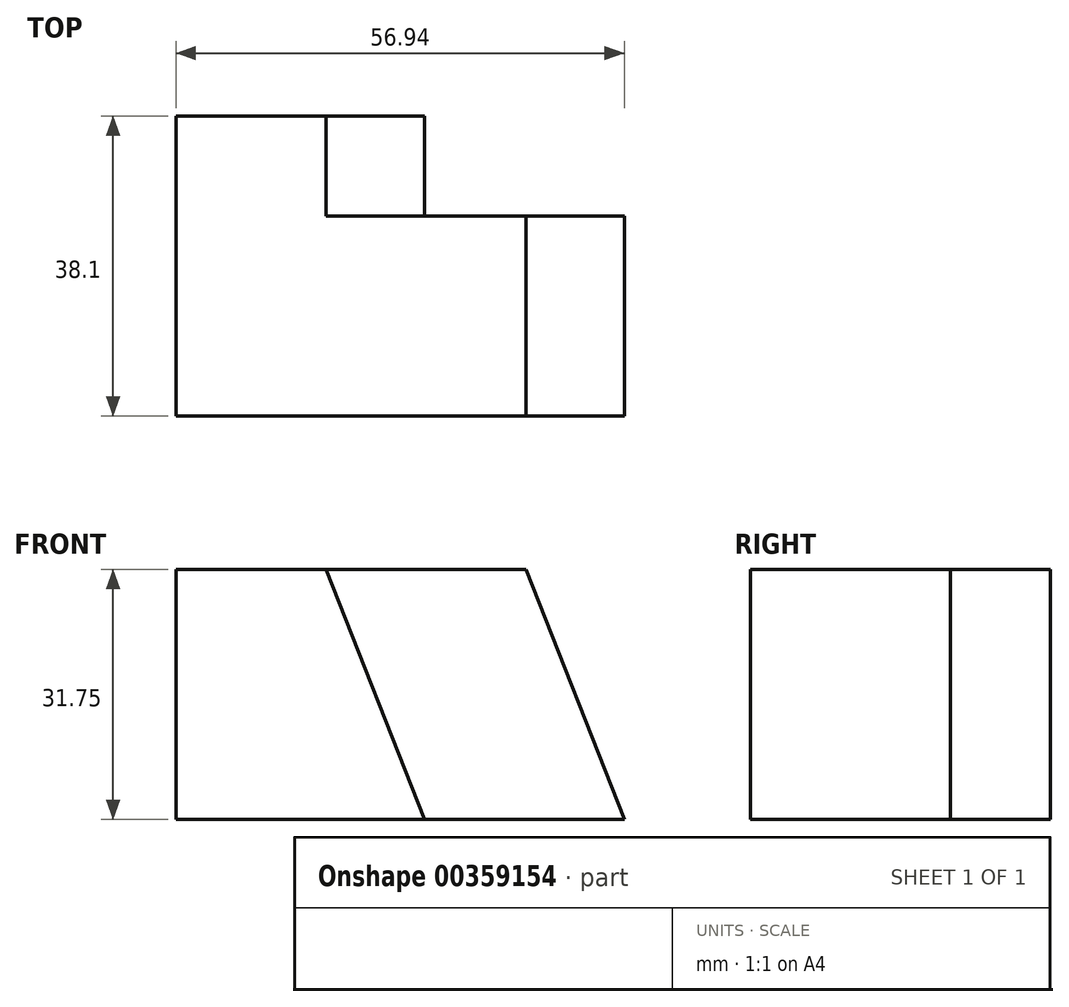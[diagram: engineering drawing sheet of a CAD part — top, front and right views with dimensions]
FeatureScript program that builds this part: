
annotation { "Feature Type Name" : "Feature", "Feature Type Description" : "" }
export const myFeature = defineFeature(function(context is Context, id is Id, definition is map)
    precondition{}
    {
        {
            var Q0;
            Q0=qCreatedBy(makeId("Front.planeOp"),FACE);
            var sketch = newSketch(context, id + "F0", { "sketchPlane" : qUnion([Q0])});
            skLineSegment(sketch, "E0", {"start": v(0, 31.75) * mm, "end": v(0, 0) * mm});
            skLineSegment(sketch, "E1", {"start": v(0, 0) * mm, "end": v(56.94, 0) * mm});
            skLineSegment(sketch, "E2", {"start": v(0, 31.75) * mm, "end": v(57.15, 31.75) * mm});
            skLineSegment(sketch, "E3", {"start": v(57.15, 31.75) * mm, "end": v(56.94, 0) * mm});
            skSolve(sketch);
        }
        {
            var Q0;
            Q0=makeQuery(id+"F0.imprint","IMPRINT",FACE,{"disambiguationData":[TD([[makeQuery(id+"F0.imprint","IMPRINT",EDGE,{"derivedFrom":sQuery(id+"F0.wireOp",EDGE,"E0")}),1.0]])]});
            extrude(context, id + "F1", {"entities" : qUnion([Q0]), "depth" : 25.4 * mm});
        }
        {
            var Q0;
            Q0=makeQuery(id+"F1.opExtrude","CAP_FACE",FACE,{"disambiguationData":[OSD([sQuery(id+"F0.wireOp",EDGE,"E0"),sQuery(id+"F0.wireOp",EDGE,"E1"),sQuery(id+"F0.wireOp",EDGE,"E2"),sQuery(id+"F0.wireOp",EDGE,"E3")])],"isStart":false});
            var sketch = newSketch(context, id + "F2", { "sketchPlane" : qUnion([Q0])});
            skLineSegment(sketch, "E4", {"start": v(56.94, 0) * mm, "end": v(44.45, 31.75) * mm});
            skSolve(sketch);
        }
        {
            var Q0;
            {var subQ0=sQuery(id+"F2.wireOp",EDGE,"E4");Q0=makeQuery(id+"F2.imprint","IMPRINT",FACE,{"disambiguationData":[TD([[makeQuery(id+"F2.imprint","IMPRINT",EDGE,{"derivedFrom":subQ0}),-1.0]])]});}
            extrude(context, id + "F3", {"entities" : qUnion([Q0]), "operationType" : NewBodyOperationType.REMOVE, "oppositeDirection" : true, "depth" : 38.1 * mm});
        }
        {
            var Q0;
            Q0=makeQuery(id+"F1.opExtrude","CAP_FACE",FACE,{"disambiguationData":[OSD([sQuery(id+"F0.wireOp",EDGE,"E0"),sQuery(id+"F0.wireOp",EDGE,"E1"),sQuery(id+"F0.wireOp",EDGE,"E2"),sQuery(id+"F0.wireOp",EDGE,"E3")])],"isStart":false});
            var sketch = newSketch(context, id + "F4", { "sketchPlane" : qUnion([Q0])});
            skLineSegment(sketch, "E5", {"start": v(19.05, 31.75) * mm, "end": v(31.54, 0) * mm});
            skSolve(sketch);
        }
        {
            var Q0;
            {var subQ0=sQuery(id+"F4.wireOp",EDGE,"E5");Q0=makeQuery(id+"F4.imprint","IMPRINT",FACE,{"disambiguationData":[TD([[makeQuery(id+"F4.imprint","IMPRINT",EDGE,{"derivedFrom":subQ0}),1.0]])]});}
            extrude(context, id + "F5", {"entities" : qUnion([Q0]), "operationType" : NewBodyOperationType.REMOVE, "oppositeDirection" : true, "depth" : 2 / 101.6 * mm});
        }
        {
            var Q0;
            Q0=makeQuery(id+"F1.opExtrude","CAP_FACE",FACE,{"disambiguationData":[OSD([sQuery(id+"F0.wireOp",EDGE,"E0"),sQuery(id+"F0.wireOp",EDGE,"E1"),sQuery(id+"F0.wireOp",EDGE,"E2"),sQuery(id+"F0.wireOp",EDGE,"E3")])],"isStart":true});
            extrude(context, id + "F6", {"entities" : qUnion([Q0]), "operationType" : NewBodyOperationType.ADD, "depth" : 12.7 * mm});
        }
        {
            var Q0;
            Q0=makeQuery(id+"F6.opExtrude","CAP_FACE",FACE,{"disambiguationData":[OSD([sQuery(id+"F0.wireOp",EDGE,"E0"),sQuery(id+"F0.wireOp",EDGE,"E1"),sQuery(id+"F0.wireOp",EDGE,"E2"),sQuery(id+"F0.wireOp",EDGE,"E3")])],"isStart":false});
            var sketch = newSketch(context, id + "F7", { "sketchPlane" : qUnion([Q0])});
            skLineSegment(sketch, "E6", {"start": v(-31.54, 0) * mm, "end": v(-19.05, 31.75) * mm});
            skSolve(sketch);
        }
        {
            var Q0;
            {var subQ0=sQuery(id+"F7.wireOp",EDGE,"E6");Q0=makeQuery(id+"F7.imprint","IMPRINT",FACE,{"disambiguationData":[TD([[makeQuery(id+"F7.imprint","IMPRINT",EDGE,{"derivedFrom":subQ0}),1.0]])]});}
            extrude(context, id + "F8", {"entities" : qUnion([Q0]), "operationType" : NewBodyOperationType.REMOVE, "oppositeDirection" : true, "depth" : 12.7 * mm});
        }
    });
